# Revit family: Geräteeinsätze GES_Geräteeinsatz_Revisionsabdeckung ZESR4
name_source: partatom
category: Generic Models
revit_build: Autodesk Revit 2015 (Build: 20140606_1530(x64)
units: mm (PartAtom-declared; Revit-internal decimal feet)

## types (3) — shared parameters
Bodenbelagdicke = 5 mm  [stored 0.0164042 ft]
Diameter dimesion = 214 mm  [stored 0.7021 ft]
Height = 33 mm  [stored 0.108268 ft]
Inner cut = 206 mm  [stored 0.675853 ft]
Inner cut 3 = 153 mm  [stored 0.501969 ft]
Inner cut2 = 165 mm
Manufacturer = OBO Bettermann
Outer Diameter Dimension = 234 mm  [stored 0.767717 ft]
URL = http://www.obo-bettermann.com

## per-type parameters (varying)
| type | GTIN | Manufacturer Art. No. | Material |
| ZESR4 U 7011 | 4012195109549 | 7406772 | Plastic RAL 7011 |
| ZESR4 U 9011 | 4012195109556 | 7406776 | Plastic RAL 9011 |
| ZESR4 U 1019 | 4012195109563 | 7406780 | Plastic RAL 1019 |

note: column(s) folded — value = type name in every type: Article Type

note: [stored X ft] marks values corroborated as IEEE doubles in the binary element streams (Revit-internal decimal feet)

## geometry (parser evidence)
native form markers: Sweep x2
no freeform markers — native parametric forms only
